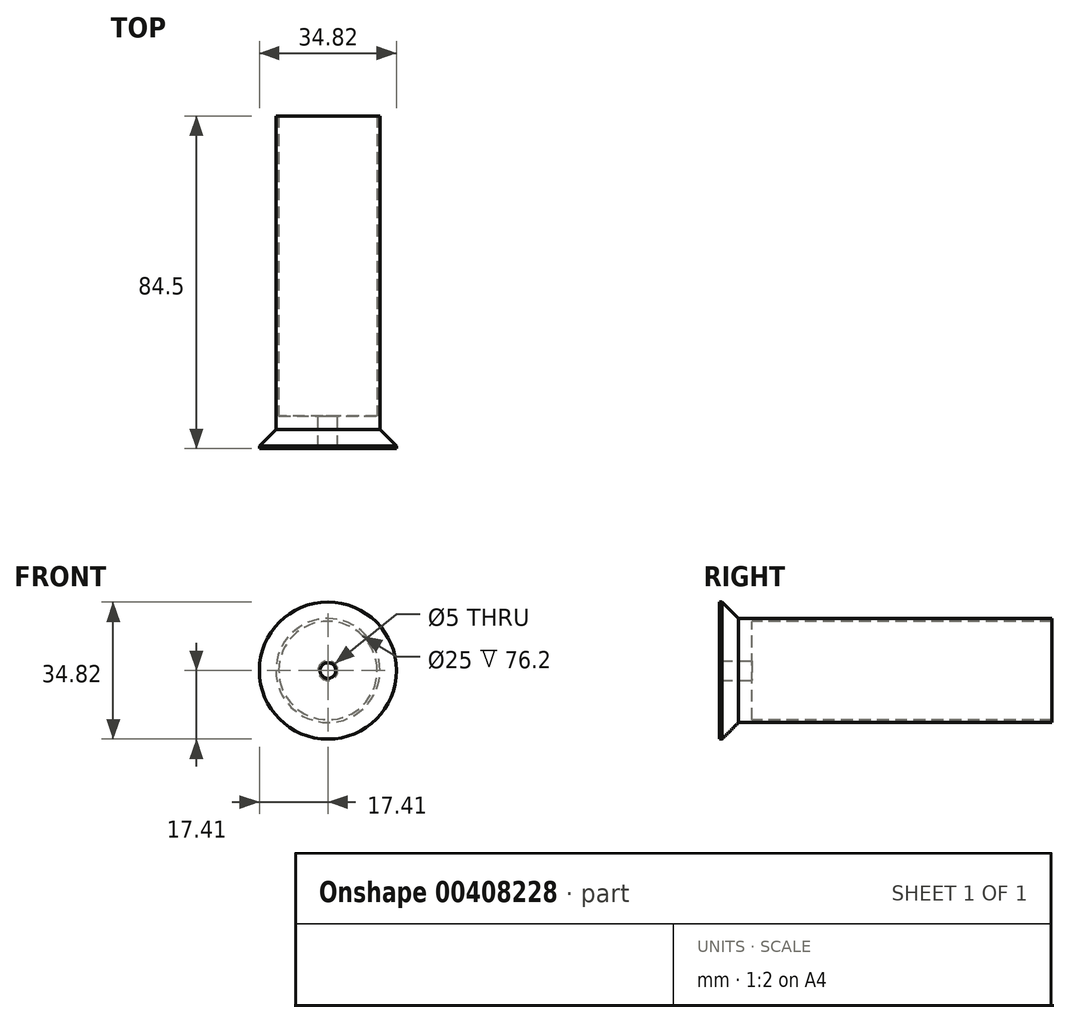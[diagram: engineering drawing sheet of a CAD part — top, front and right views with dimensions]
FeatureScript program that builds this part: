
annotation { "Feature Type Name" : "Feature", "Feature Type Description" : "" }
export const myFeature = defineFeature(function(context is Context, id is Id, definition is map)
    precondition{}
    {
        {
            var Q0;
            Q0=qCreatedBy(makeId("Front.planeOp"),FACE);
            var sketch = newSketch(context, id + "F0", { "sketchPlane" : qUnion([Q0])});
            skCircle(sketch, "E0", {"center": v(0, 0) * mm, "radius": 13.2 * mm});
            skSolve(sketch);
        }
        {
            var Q0;
            Q0=makeQuery(id+"F0.imprint","IMPRINT",FACE,{"disambiguationData":[TD([[makeQuery(id+"F0.imprint","IMPRINT",EDGE,{"derivedFrom":sQuery(id+"F0.wireOp",EDGE,"E0")}),1.0]])]});
            extrude(context, id + "F1", {"entities" : qUnion([Q0]), "oppositeDirection" : true, "depth" : 76.2 * mm});
        }
        {
            var Q0;
            Q0=qCreatedBy(makeId("Front.planeOp"),FACE);
            var sketch = newSketch(context, id + "F2", { "sketchPlane" : qUnion([Q0])});
            skCircle(sketch, "E1", {"center": v(0, 0) * mm, "radius": 17.4 * mm});
            skSolve(sketch);
        }
        {
            var Q0;
            Q0=makeQuery(id+"F2.imprint","IMPRINT",FACE,{"disambiguationData":[TD([[makeQuery(id+"F2.imprint","IMPRINT",EDGE,{"derivedFrom":sQuery(id+"F2.wireOp",EDGE,"E1")}),1.0]])]});
            extrude(context, id + "F3", {"entities" : qUnion([Q0]), "operationType" : NewBodyOperationType.ADD, "depth" : 8.3 * mm});
        }
        {
            var Q0;
            Q0=makeQuery(id+"F3.opExtrude","CAP_EDGE",EDGE,{"disambiguationData":[OSD([sQuery(id+"F2.wireOp",EDGE,"E1")])],"isStart":true});
            chamfer(context, id + "F4", {"entities" : qUnion([Q0]), "width" : 7.62 * mm, "tangentPropagation" : true});
        }
        {
            var Q0;
            Q0=qCreatedBy(makeId("Front.planeOp"),FACE);
            var sketch = newSketch(context, id + "F5", { "sketchPlane" : qUnion([Q0])});
            skPoint(sketch, "E2", {"position": v(0, 0) * mm});
            skSolve(sketch);
        }
        {
            var Q0;
            Q0=sQuery(id+"F5.wireOp",VERTEX,"E2");
            var Q1;
            Q1=makeQuery(id+"F1.opExtrude","SWEPT_BODY",BODY,{"disambiguationData":[OSD([sQuery(id+"F0.wireOp",EDGE,"E0")])]});
            hole(context, id + "F6", {"style" : HoleStyle.SIMPLE, "endStyle" : HoleEndStyle.BLIND, "oppositeDirection" : true, "holeDiameter" : 5 * mm, "holeDepth" : 8 * mm, "isTappedThrough" : true, "tappedDepth" : 12 * mm, "tapClearance" : 3, "locations" : qUnion([Q0]), "scope" : qUnion([Q1])});
        }
        {
            var Q0;
            Q0=qCreatedBy(makeId("Front.planeOp"),FACE);
            var sketch = newSketch(context, id + "F7", { "sketchPlane" : qUnion([Q0])});
            skCircle(sketch, "E3", {"center": v(0, 0) * mm, "radius": 12.46 * mm});
            skSolve(sketch);
        }
        {
            var Q0;
            Q0=qCreatedBy(makeId("Front.planeOp"),FACE);
            var sketch = newSketch(context, id + "F8", { "sketchPlane" : qUnion([Q0])});
            skPoint(sketch, "E4", {"position": v(0, 0) * mm});
            skSolve(sketch);
        }
        {
            var Q0;
            Q0=sQuery(id+"F7.wireOp",VERTEX,"E3.center");
            var Q1;
            Q1=sQuery(id+"F8.wireOp",VERTEX,"E4");
            var Q2;
            Q2=makeQuery(id+"F1.opExtrude","SWEPT_BODY",BODY,{"disambiguationData":[OSD([sQuery(id+"F0.wireOp",EDGE,"E0")])]});
            hole(context, id + "F9", {"style" : HoleStyle.SIMPLE, "endStyle" : HoleEndStyle.THROUGH, "holeDiameter" : 25 * mm, "isTappedThrough" : true, "tappedDepth" : 12 * mm, "tapClearance" : 3, "locations" : qUnion([Q0, Q1]), "scope" : qUnion([Q2])});
        }
    });
